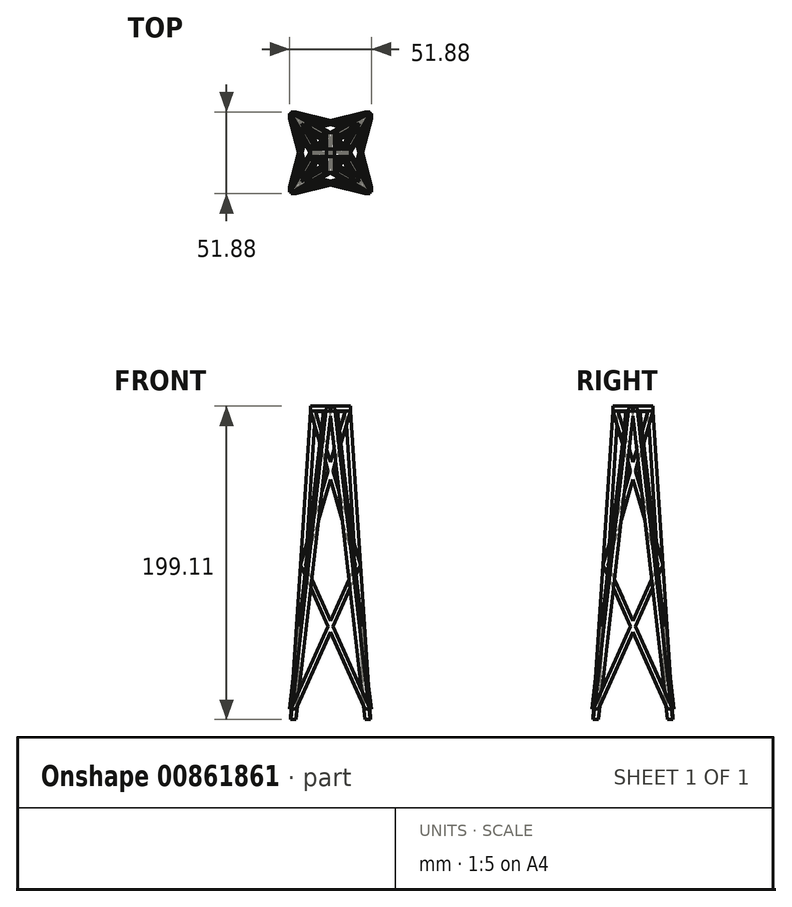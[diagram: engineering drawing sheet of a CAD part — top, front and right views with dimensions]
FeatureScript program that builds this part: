
annotation { "Feature Type Name" : "Feature", "Feature Type Description" : "" }
export const myFeature = defineFeature(function(context is Context, id is Id, definition is map)
    precondition{}
    {
        {
            var Q0;
            Q0=qCreatedBy(makeId("Top.planeOp"),FACE);
            var sketch = newSketch(context, id + "F0", { "sketchPlane" : qUnion([Q0])});
            skLineSegment(sketch, "E0", {"start": v(0, 0) * mm, "end": v(0, 116.82) * mm, "construction": true});
            skLineSegment(sketch, "E1", {"start": v(0, 0) * mm, "end": v(-140.82, 0) * mm, "construction": true});
            skSolve(sketch);
        }
        {
            var Q0;
            Q0=qCreatedBy(makeId("Right.planeOp"),FACE);
            var sketch = newSketch(context, id + "F1", { "sketchPlane" : qUnion([Q0])});
            skLineSegment(sketch, "E2", {"start": v(0, 0) * mm, "end": v(0, 190.5) * mm, "construction": true});
            skSolve(sketch);
        }
        {
            var Q0;
            Q0=qCreatedBy(makeId("Right.planeOp"),FACE);
            var sketch = newSketch(context, id + "F2", { "sketchPlane" : qUnion([Q0])});
            skPoint(sketch, "E3", {"position": v(-25.4, 0) * mm});
            skPoint(sketch, "E4.MirrorP", {"position": v(25.4, 0) * mm});
            skPoint(sketch, "E5", {"position": v(0, 215.9) * mm});
            skLineSegment(sketch, "E6", {"start": v(-25.4, 0) * mm, "end": v(0, 223.32) * mm, "construction": true});
            skSolve(sketch);
        }
        {
            var Q0;
            Q0=qBodyType(qCreatedBy(id+"F2",EDGE),BodyType.WIRE);
            cPlane(context, id + "F3", {"entities" : qUnion([Q0]), "cplaneType" : CPlaneType.LINE_ANGLE, "offset" : 25.4 * mm, "angle" : 90 * degree, "oppositeDirection" : true, "width" : 152.4 * mm, "height" : 152.4 * mm});
        }
        {
            var Q0;
            Q0=qCreatedBy(id+"F3.planeOp",FACE);
            var sketch = newSketch(context, id + "F4", { "sketchPlane" : qUnion([Q0])});
            skPoint(sketch, "E7", {"position": v(-25.4, 0) * mm});
            skPoint(sketch, "E8", {"position": v(0, 215.9) * mm});
            skPoint(sketch, "E9", {"position": v(0, 196.85) * mm});
            skLineSegment(sketch, "E10", {"start": v(-25.4, 0) * mm, "end": v(-12.7, 196.85) * mm});
            skLineSegment(sketch, "E11.0", {"start": v(-22.22, 0) * mm, "end": v(-9.52, 196.85) * mm});
            skLineSegment(sketch, "E12", {"start": v(-25.4, 0) * mm, "end": v(-22.22, 0) * mm});
            skLineSegment(sketch, "E13", {"start": v(-12.7, 196.85) * mm, "end": v(-9.52, 196.85) * mm});
            skLineSegment(sketch, "E14", {"start": v(-12.7, 200.03) * mm, "end": v(-12.7, 196.85) * mm});
            skLineSegment(sketch, "E15.MirrorCS", {"start": v(12.7, 196.85) * mm, "end": v(9.52, 196.85) * mm});
            skLineSegment(sketch, "E16.MirrorCS", {"start": v(12.7, 200.03) * mm, "end": v(12.7, 196.85) * mm});
            skLineSegment(sketch, "E17.MirrorCS", {"start": v(25.4, 0) * mm, "end": v(22.22, 0) * mm});
            skLineSegment(sketch, "E18.MirrorCS", {"start": v(25.4, 0) * mm, "end": v(12.7, 196.85) * mm});
            skLineSegment(sketch, "E19.MirrorCS", {"start": v(22.22, 0) * mm, "end": v(9.52, 196.85) * mm});
            skLineSegment(sketch, "E20", {"start": v(-12.7, 196.85) * mm, "end": v(12.7, 196.85) * mm});
            skLineSegment(sketch, "E21", {"start": v(-12.7, 200.03) * mm, "end": v(12.7, 200.03) * mm});
            skLineSegment(sketch, "E22", {"start": v(-65.08, 200.03) * mm, "end": v(-65.08, 0) * mm, "construction": true});
            skLineSegment(sketch, "E23", {"start": v(-59.43, 196.85) * mm, "end": v(-59.43, 0) * mm, "construction": true});
            skLineSegment(sketch, "E24", {"start": v(-59.43, 98.43) * mm, "end": v(114.07, 98.43) * mm, "construction": true});
            skLineSegment(sketch, "E25", {"start": v(-44.46, 6.35) * mm, "end": v(-44.46, 0) * mm, "construction": true});
            skLineSegment(sketch, "E26", {"start": v(-25, 6.35) * mm, "end": v(15.87, 98.43) * mm});
            skLineSegment(sketch, "E27", {"start": v(15.87, 98.43) * mm, "end": v(19.05, 98.43) * mm});
            skLineSegment(sketch, "E28", {"start": v(19.05, 98.42) * mm, "end": v(-21.8, 6.35) * mm});
            skLineSegment(sketch, "E29", {"start": v(-21.8, 6.35) * mm, "end": v(-25, 6.35) * mm});
            skLineSegment(sketch, "E30", {"start": v(-9.52, 196.85) * mm, "end": v(19.05, 98.42) * mm});
            skLineSegment(sketch, "E31", {"start": v(15.87, 98.43) * mm, "end": v(-12.7, 196.85) * mm});
            skLineSegment(sketch, "E32", {"start": v(9.52, 196.85) * mm, "end": v(-19.05, 98.43) * mm});
            skLineSegment(sketch, "E33", {"start": v(-19.05, 98.43) * mm, "end": v(-15.88, 98.22) * mm});
            skLineSegment(sketch, "E34", {"start": v(-15.88, 98.22) * mm, "end": v(12.7, 196.85) * mm});
            skLineSegment(sketch, "E35", {"start": v(21.8, 6.35) * mm, "end": v(-19.05, 98.43) * mm});
            skLineSegment(sketch, "E36", {"start": v(-15.88, 98.22) * mm, "end": v(25, 6.35) * mm});
            skLineSegment(sketch, "E37", {"start": v(25, 6.35) * mm, "end": v(21.8, 6.35) * mm});
            skSolve(sketch);
        }
        {
            var Q0;
            {var subQ2=sQuery(id+"F4.wireOp",EDGE,"E12");Q0=makeQuery(id+"F4.imprint","IMPRINT",FACE,{"disambiguationData":[TD([[makeQuery(id+"F4.imprint","IMPRINT",EDGE,{"derivedFrom":subQ2}),1.0]])]});}
            var Q1;
            {var subQ0=sQuery(id+"F4.wireOp",EDGE,"E17.MirrorCS");Q1=makeQuery(id+"F4.imprint","IMPRINT",FACE,{"disambiguationData":[TD([[makeQuery(id+"F4.imprint","IMPRINT",EDGE,{"derivedFrom":subQ0}),-1.0]])]});}
            var Q2;
            {var subQ3=sQuery(id+"F4.wireOp",EDGE,"E26");var subQ5=sQuery(id+"F4.wireOp",EDGE,"E11.0");var subQ7=makeQuery(id+"F4.imprint","INTERSECT",VERTEX,{"derivedFrom":[subQ5,subQ3]});Q2=makeQuery(id+"F4.imprint","IMPRINT",FACE,{"disambiguationData":[TD([[makeQuery(id+"F4.imprint","IMPRINT",EDGE,{"disambiguationData":[TD([[subQ7,-1.0]])],"derivedFrom":subQ5}),1.0]])]});}
            var Q3;
            {var subQ0=sQuery(id+"F4.wireOp",EDGE,"E32");var subQ5=sQuery(id+"F4.wireOp",EDGE,"E11.0");var subQ6=makeQuery(id+"F4.imprint","INTERSECT",VERTEX,{"derivedFrom":[subQ5,subQ0]});Q3=makeQuery(id+"F4.imprint","IMPRINT",FACE,{"disambiguationData":[TD([[makeQuery(id+"F4.imprint","IMPRINT",EDGE,{"disambiguationData":[TD([[subQ6,-1.0]])],"derivedFrom":subQ5}),1.0]])]});}
            var Q4;
            {var subQ3=sQuery(id+"F4.wireOp",EDGE,"E29");Q4=makeQuery(id+"F4.imprint","IMPRINT",FACE,{"disambiguationData":[TD([[makeQuery(id+"F4.imprint","IMPRINT",EDGE,{"derivedFrom":subQ3}),-1.0]])]});}
            var Q5;
            {var subQ0=sQuery(id+"F4.wireOp",EDGE,"E33");Q5=makeQuery(id+"F4.imprint","IMPRINT",FACE,{"disambiguationData":[TD([[makeQuery(id+"F4.imprint","IMPRINT",EDGE,{"derivedFrom":subQ0}),-1.0]])]});}
            var Q6;
            {var subQ0=sQuery(id+"F4.wireOp",EDGE,"E33");Q6=makeQuery(id+"F4.imprint","IMPRINT",FACE,{"disambiguationData":[TD([[makeQuery(id+"F4.imprint","IMPRINT",EDGE,{"derivedFrom":subQ0}),1.0]])]});}
            var Q7;
            {var subQ5=sQuery(id+"F4.wireOp",EDGE,"E13");Q7=makeQuery(id+"F4.imprint","IMPRINT",FACE,{"disambiguationData":[TD([[makeQuery(id+"F4.imprint","IMPRINT",EDGE,{"derivedFrom":subQ5}),-1.0]])]});}
            var Q8;
            {var subQ3=sQuery(id+"F4.wireOp",EDGE,"E36");var subQ5=sQuery(id+"F4.wireOp",EDGE,"E19.MirrorCS");var subQ6=makeQuery(id+"F4.imprint","INTERSECT",VERTEX,{"derivedFrom":[subQ5,subQ3]});Q8=makeQuery(id+"F4.imprint","IMPRINT",FACE,{"disambiguationData":[TD([[makeQuery(id+"F4.imprint","IMPRINT",EDGE,{"disambiguationData":[TD([[subQ6,-1.0]])],"derivedFrom":subQ5}),-1.0]])]});}
            var Q9;
            {var subQ3=sQuery(id+"F4.wireOp",EDGE,"E30");var subQ5=sQuery(id+"F4.wireOp",EDGE,"E19.MirrorCS");var subQ6=makeQuery(id+"F4.imprint","INTERSECT",VERTEX,{"derivedFrom":[subQ5,subQ3]});Q9=makeQuery(id+"F4.imprint","IMPRINT",FACE,{"disambiguationData":[TD([[makeQuery(id+"F4.imprint","IMPRINT",EDGE,{"disambiguationData":[TD([[subQ6,-1.0]])],"derivedFrom":subQ5}),-1.0]])]});}
            var Q10;
            {var subQ3=sQuery(id+"F4.wireOp",EDGE,"E37");Q10=makeQuery(id+"F4.imprint","IMPRINT",FACE,{"disambiguationData":[TD([[makeQuery(id+"F4.imprint","IMPRINT",EDGE,{"derivedFrom":subQ3}),-1.0]])]});}
            var Q11;
            {var subQ0=sQuery(id+"F4.wireOp",EDGE,"E27");Q11=makeQuery(id+"F4.imprint","IMPRINT",FACE,{"disambiguationData":[TD([[makeQuery(id+"F4.imprint","IMPRINT",EDGE,{"derivedFrom":subQ0}),-1.0]])]});}
            var Q12;
            {var subQ0=sQuery(id+"F4.wireOp",EDGE,"E27");Q12=makeQuery(id+"F4.imprint","IMPRINT",FACE,{"disambiguationData":[TD([[makeQuery(id+"F4.imprint","IMPRINT",EDGE,{"derivedFrom":subQ0}),1.0]])]});}
            var Q13;
            {var subQ1=sQuery(id+"F4.wireOp",EDGE,"E13");Q13=makeQuery(id+"F4.imprint","IMPRINT",FACE,{"disambiguationData":[TD([[makeQuery(id+"F4.imprint","IMPRINT",EDGE,{"derivedFrom":subQ1}),1.0]])]});}
            var Q14;
            {var subQ0=sQuery(id+"F4.wireOp",EDGE,"E15.MirrorCS");Q14=makeQuery(id+"F4.imprint","IMPRINT",FACE,{"disambiguationData":[TD([[makeQuery(id+"F4.imprint","IMPRINT",EDGE,{"derivedFrom":subQ0}),1.0]])]});}
            extrude(context, id + "F5", {"entities" : qUnion([Q0, Q1, Q2, Q3, Q4, Q5, Q6, Q7, Q8, Q9, Q10, Q11, Q12, Q13, Q14]), "oppositeDirection" : true, "depth" : 3.17 * mm, "offsetDistance" : 25.4 * mm});
        }
        {
            var Q0;
            {var subQ5=sQuery(id+"F4.wireOp",EDGE,"E13");Q0=makeQuery(id+"F4.imprint","IMPRINT",FACE,{"disambiguationData":[TD([[makeQuery(id+"F4.imprint","IMPRINT",EDGE,{"derivedFrom":subQ5}),-1.0]])]});}
            var Q1;
            {var subQ3=sQuery(id+"F4.wireOp",EDGE,"E31");var subQ5=sQuery(id+"F4.wireOp",EDGE,"E32");var subQ6=makeQuery(id+"F4.imprint","INTERSECT",VERTEX,{"derivedFrom":[subQ3,subQ5]});Q1=makeQuery(id+"F4.imprint","IMPRINT",FACE,{"disambiguationData":[TD([[makeQuery(id+"F4.imprint","IMPRINT",EDGE,{"disambiguationData":[TD([[subQ6,-1.0]])],"derivedFrom":subQ3}),-1.0]])]});}
            var Q2;
            {var subQ0=sQuery(id+"F4.wireOp",EDGE,"E32");var subQ1=sQuery(id+"F4.wireOp",EDGE,"E19.MirrorCS");var subQ2=makeQuery(id+"F4.imprint","INTERSECT",VERTEX,{"derivedFrom":[subQ1,subQ0]});Q2=makeQuery(id+"F4.imprint","IMPRINT",FACE,{"disambiguationData":[TD([[makeQuery(id+"F4.imprint","IMPRINT",EDGE,{"disambiguationData":[TD([[subQ2,1.0]])],"derivedFrom":subQ1}),1.0]])]});}
            var Q3;
            {var subQ0=sQuery(id+"F4.wireOp",EDGE,"E15.MirrorCS");Q3=makeQuery(id+"F4.imprint","IMPRINT",FACE,{"disambiguationData":[TD([[makeQuery(id+"F4.imprint","IMPRINT",EDGE,{"derivedFrom":subQ0}),1.0]])]});}
            var Q4;
            {var subQ0=sQuery(id+"F4.wireOp",EDGE,"E34");var subQ1=sQuery(id+"F4.wireOp",EDGE,"E30");var subQ2=makeQuery(id+"F4.imprint","INTERSECT",VERTEX,{"derivedFrom":[subQ1,subQ0]});Q4=makeQuery(id+"F4.imprint","IMPRINT",FACE,{"disambiguationData":[TD([[makeQuery(id+"F4.imprint","IMPRINT",EDGE,{"disambiguationData":[TD([[subQ2,1.0]])],"derivedFrom":subQ1}),-1.0]])]});}
            var Q5;
            {var subQ3=sQuery(id+"F4.wireOp",EDGE,"E32");var subQ5=sQuery(id+"F4.wireOp",EDGE,"E31");var subQ7=makeQuery(id+"F4.imprint","INTERSECT",VERTEX,{"derivedFrom":[subQ5,subQ3]});Q5=makeQuery(id+"F4.imprint","IMPRINT",FACE,{"disambiguationData":[TD([[makeQuery(id+"F4.imprint","IMPRINT",EDGE,{"disambiguationData":[TD([[subQ7,1.0]])],"derivedFrom":subQ5}),1.0]])]});}
            var Q6;
            {var subQ0=sQuery(id+"F4.wireOp",EDGE,"E33");Q6=makeQuery(id+"F4.imprint","IMPRINT",FACE,{"disambiguationData":[TD([[makeQuery(id+"F4.imprint","IMPRINT",EDGE,{"derivedFrom":subQ0}),1.0]])]});}
            var Q7;
            {var subQ3=sQuery(id+"F4.wireOp",EDGE,"E30");var subQ5=sQuery(id+"F4.wireOp",EDGE,"E34");var subQ6=makeQuery(id+"F4.imprint","INTERSECT",VERTEX,{"derivedFrom":[subQ3,subQ5]});Q7=makeQuery(id+"F4.imprint","IMPRINT",FACE,{"disambiguationData":[TD([[makeQuery(id+"F4.imprint","IMPRINT",EDGE,{"disambiguationData":[TD([[subQ6,-1.0]])],"derivedFrom":subQ3}),-1.0]])]});}
            var Q8;
            {var subQ0=sQuery(id+"F4.wireOp",EDGE,"E27");Q8=makeQuery(id+"F4.imprint","IMPRINT",FACE,{"disambiguationData":[TD([[makeQuery(id+"F4.imprint","IMPRINT",EDGE,{"derivedFrom":subQ0}),1.0]])]});}
            var Q9;
            {var subQ3=sQuery(id+"F4.wireOp",EDGE,"E28");var subQ5=sQuery(id+"F4.wireOp",EDGE,"E36");var subQ7=makeQuery(id+"F4.imprint","INTERSECT",VERTEX,{"derivedFrom":[subQ3,subQ5]});Q9=makeQuery(id+"F4.imprint","IMPRINT",FACE,{"disambiguationData":[TD([[makeQuery(id+"F4.imprint","IMPRINT",EDGE,{"disambiguationData":[TD([[subQ7,1.0]])],"derivedFrom":subQ3}),-1.0]])]});}
            var Q10;
            {var subQ0=sQuery(id+"F4.wireOp",EDGE,"E27");Q10=makeQuery(id+"F4.imprint","IMPRINT",FACE,{"disambiguationData":[TD([[makeQuery(id+"F4.imprint","IMPRINT",EDGE,{"derivedFrom":subQ0}),-1.0]])]});}
            var Q11;
            {var subQ0=sQuery(id+"F4.wireOp",EDGE,"E36");var subQ5=sQuery(id+"F4.wireOp",EDGE,"E26");var subQ6=makeQuery(id+"F4.imprint","INTERSECT",VERTEX,{"derivedFrom":[subQ5,subQ0]});Q11=makeQuery(id+"F4.imprint","IMPRINT",FACE,{"disambiguationData":[TD([[makeQuery(id+"F4.imprint","IMPRINT",EDGE,{"disambiguationData":[TD([[subQ6,1.0]])],"derivedFrom":subQ5}),1.0]])]});}
            var Q12;
            {var subQ0=sQuery(id+"F4.wireOp",EDGE,"E33");Q12=makeQuery(id+"F4.imprint","IMPRINT",FACE,{"disambiguationData":[TD([[makeQuery(id+"F4.imprint","IMPRINT",EDGE,{"derivedFrom":subQ0}),-1.0]])]});}
            var Q13;
            {var subQ0=sQuery(id+"F4.wireOp",EDGE,"E36");var subQ1=sQuery(id+"F4.wireOp",EDGE,"E26");var subQ2=makeQuery(id+"F4.imprint","INTERSECT",VERTEX,{"derivedFrom":[subQ1,subQ0]});Q13=makeQuery(id+"F4.imprint","IMPRINT",FACE,{"disambiguationData":[TD([[makeQuery(id+"F4.imprint","IMPRINT",EDGE,{"disambiguationData":[TD([[subQ2,1.0]])],"derivedFrom":subQ1}),-1.0]])]});}
            var Q14;
            {var subQ3=sQuery(id+"F4.wireOp",EDGE,"E35");var subQ5=sQuery(id+"F4.wireOp",EDGE,"E28");var subQ7=makeQuery(id+"F4.imprint","INTERSECT",VERTEX,{"derivedFrom":[subQ5,subQ3]});Q14=makeQuery(id+"F4.imprint","IMPRINT",FACE,{"disambiguationData":[TD([[makeQuery(id+"F4.imprint","IMPRINT",EDGE,{"disambiguationData":[TD([[subQ7,1.0]])],"derivedFrom":subQ5}),1.0]])]});}
            var Q15;
            {var subQ0=sQuery(id+"F4.wireOp",EDGE,"E26");var subQ1=sQuery(id+"F4.wireOp",EDGE,"E11.0");var subQ2=makeQuery(id+"F4.imprint","INTERSECT",VERTEX,{"derivedFrom":[subQ1,subQ0]});Q15=makeQuery(id+"F4.imprint","IMPRINT",FACE,{"disambiguationData":[TD([[makeQuery(id+"F4.imprint","IMPRINT",EDGE,{"disambiguationData":[TD([[subQ2,-1.0]])],"derivedFrom":subQ0}),-1.0]])]});}
            var Q16;
            {var subQ3=sQuery(id+"F4.wireOp",EDGE,"E37");Q16=makeQuery(id+"F4.imprint","IMPRINT",FACE,{"disambiguationData":[TD([[makeQuery(id+"F4.imprint","IMPRINT",EDGE,{"derivedFrom":subQ3}),-1.0]])]});}
            var Q17;
            {var subQ3=sQuery(id+"F4.wireOp",EDGE,"E29");Q17=makeQuery(id+"F4.imprint","IMPRINT",FACE,{"disambiguationData":[TD([[makeQuery(id+"F4.imprint","IMPRINT",EDGE,{"derivedFrom":subQ3}),-1.0]])]});}
            extrude(context, id + "F6", {"entities" : qUnion([Q0, Q1, Q2, Q3, Q4, Q5, Q6, Q7, Q8, Q9, Q10, Q11, Q12, Q13, Q14, Q15, Q16, Q17]), "operationType" : NewBodyOperationType.ADD, "depth" : 1.59 * mm, "offsetDistance" : 25.4 * mm});
        }
        {
            var Q0;
            Q0=makeQuery(id+"F5.opExtrude","SWEPT_BODY",BODY,{"disambiguationData":[OSD([sQuery(id+"F4.wireOp",EDGE,"E10"),sQuery(id+"F4.wireOp",EDGE,"E11.0"),sQuery(id+"F4.wireOp",EDGE,"E12"),sQuery(id+"F4.wireOp",EDGE,"E14"),sQuery(id+"F4.wireOp",EDGE,"E16.MirrorCS"),sQuery(id+"F4.wireOp",EDGE,"E17.MirrorCS"),sQuery(id+"F4.wireOp",EDGE,"E18.MirrorCS"),sQuery(id+"F4.wireOp",EDGE,"E19.MirrorCS"),sQuery(id+"F4.wireOp",EDGE,"E20"),sQuery(id+"F4.wireOp",EDGE,"E21"),sQuery(id+"F4.wireOp",EDGE,"E32")])]});
            var Q1;
            Q1=sQuery(id+"F1.wireOp",EDGE,"E2");
            circularPattern(context, id + "F7", {"entities" : qUnion([Q0]), "axis" : qUnion([Q1]), "angle" : 360 * degree, "instanceCount" : 4, "oppositeDirection" : true, "equalSpace" : true, "isCentered" : true});
        }
    });
